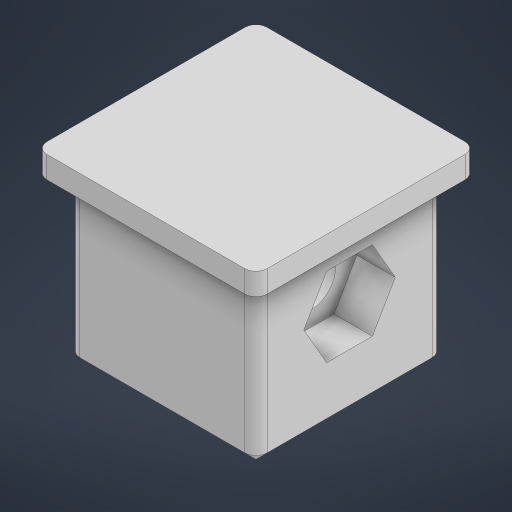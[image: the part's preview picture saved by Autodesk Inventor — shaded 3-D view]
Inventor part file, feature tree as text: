
AUTODESK INVENTOR PART (.ipt)
format: ipt  version: 2024 (Build 280153000, 153)  size: 242,688 bytes
history: native  units: mm
features: extrude x4, sketch x4, other x2, mirror x1, shell x1, fillet x1, chamfer x1
ambient origin geometry x8: Origin, YZ Plane, XZ Plane, XY Plane, X Axis, Y Axis, Z Axis, Center Point
bodies: Body1 (feature_tree)
feature tree (14):
  other  "Твердое тело1"
  extrude  "Выдавливание1"  Depth=17.0mm
  extrude  "Выдавливание2"  Depth=17.0mm
  other  "РабПлоскость1"
  mirror  "Зеркальное отражение1"
  shell  "Оболочка1"  Thickness=15.0mm
  extrude  "Выдавливание3"  Depth=7.2mm
  fillet  "Сопряжение1"  Radius=3.5mm
  chamfer  "Фаска1"  Distance=3.5mm
  extrude  "Выдавливание4"  Depth=20.0mm
  sketch  "Эскиз1"
  sketch  "Эскиз2"
  sketch  "Эскиз3"
  sketch  "Эскиз4"
